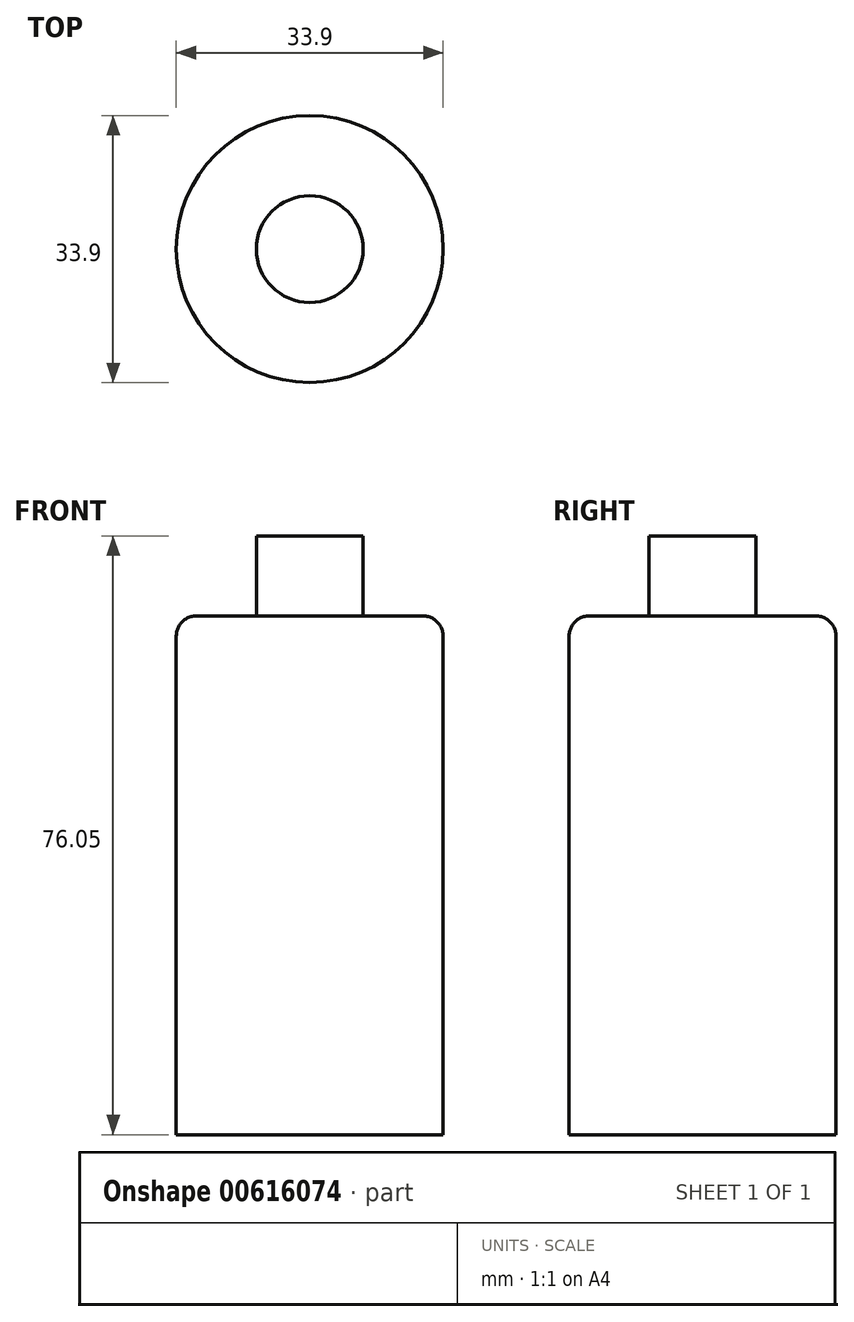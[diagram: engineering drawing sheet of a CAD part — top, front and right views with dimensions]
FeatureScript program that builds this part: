
annotation { "Feature Type Name" : "Feature", "Feature Type Description" : "" }
export const myFeature = defineFeature(function(context is Context, id is Id, definition is map)
    precondition{}
    {
        {
            var Q0;
            Q0=qCreatedBy(makeId("Front.planeOp"),FACE);
            var sketch = newSketch(context, id + "F0", { "sketchPlane" : qUnion([Q0])});
            skLineSegment(sketch, "E0.bottom", {"start": v(0, -21.53) * mm, "end": v(16.95, -21.53) * mm});
            skLineSegment(sketch, "E0.top", {"start": v(2.54, 44.36) * mm, "end": v(16.95, 44.36) * mm});
            skLineSegment(sketch, "E0.left", {"start": v(0, -21.53) * mm, "end": v(0, 41.82) * mm});
            skLineSegment(sketch, "E0.right", {"start": v(16.95, -21.53) * mm, "end": v(16.95, 44.36) * mm});
            skPoint(sketch, "E1.visualSharp", {"position": v(0, 44.36) * mm});
            skArc(sketch, "E1.filletArc", {"start": v(2.54, 44.36) * mm, "mid": v(0.74, 43.62) * mm, "end": v(0, 41.82) * mm});
            skSolve(sketch);
        }
        {
            var Q0;
            Q0 = qSketchRegion(id + "F0", true);
            var Q1;
            Q1=sQuery(id+"F0.wireOp",EDGE,"E0.right");
            revolve(context, id + "F1", {"entities" : qUnion([Q0]), "axis" : qUnion([Q1]), "revolveType" : RevolveType.FULL});
        }
        {
            var Q0;
            Q0=makeQuery(id+"F1.opRevolve","SWEPT_FACE",FACE,{"disambiguationData":[OSD([sQuery(id+"F0.wireOp",EDGE,"E0.top")])]});
            var sketch = newSketch(context, id + "F2", { "sketchPlane" : qUnion([Q0])});
            skCircle(sketch, "E2", {"center": v(16.95, 0) * mm, "radius": 6.78 * mm});
            skSolve(sketch);
        }
        {
            var Q0;
            Q0=makeQuery(id+"F2.imprint","IMPRINT",FACE,{"disambiguationData":[TD([[makeQuery(id+"F2.imprint","IMPRINT",EDGE,{"derivedFrom":sQuery(id+"F2.wireOp",EDGE,"E2")}),1.0]])]});
            extrude(context, id + "F3", {"entities" : qUnion([Q0]), "operationType" : NewBodyOperationType.ADD, "depth" : 10.16 * mm, "offsetDistance" : 25.4 * mm});
        }
        {
            var Q0;
            Q0=makeQuery(id+"F3.opExtrude","CAP_FACE",FACE,{"disambiguationData":[OSD([sQuery(id+"F2.wireOp",EDGE,"E2")])],"isStart":false});
            var sketch = newSketch(context, id + "F4", { "sketchPlane" : qUnion([Q0])});
            skCircle(sketch, "E3", {"center": v(16.95, 0) * mm, "radius": 4.8 * mm});
            skSolve(sketch);
        }
        {
            var Q0;
            Q0 = qSketchRegion(id + "F4", true);
            extrude(context, id + "F5", {"entities" : qUnion([Q0]), "operationType" : NewBodyOperationType.ADD, "oppositeDirection" : true, "depth" : 4 * mm, "offsetDistance" : 25.4 * mm});
        }
    });
